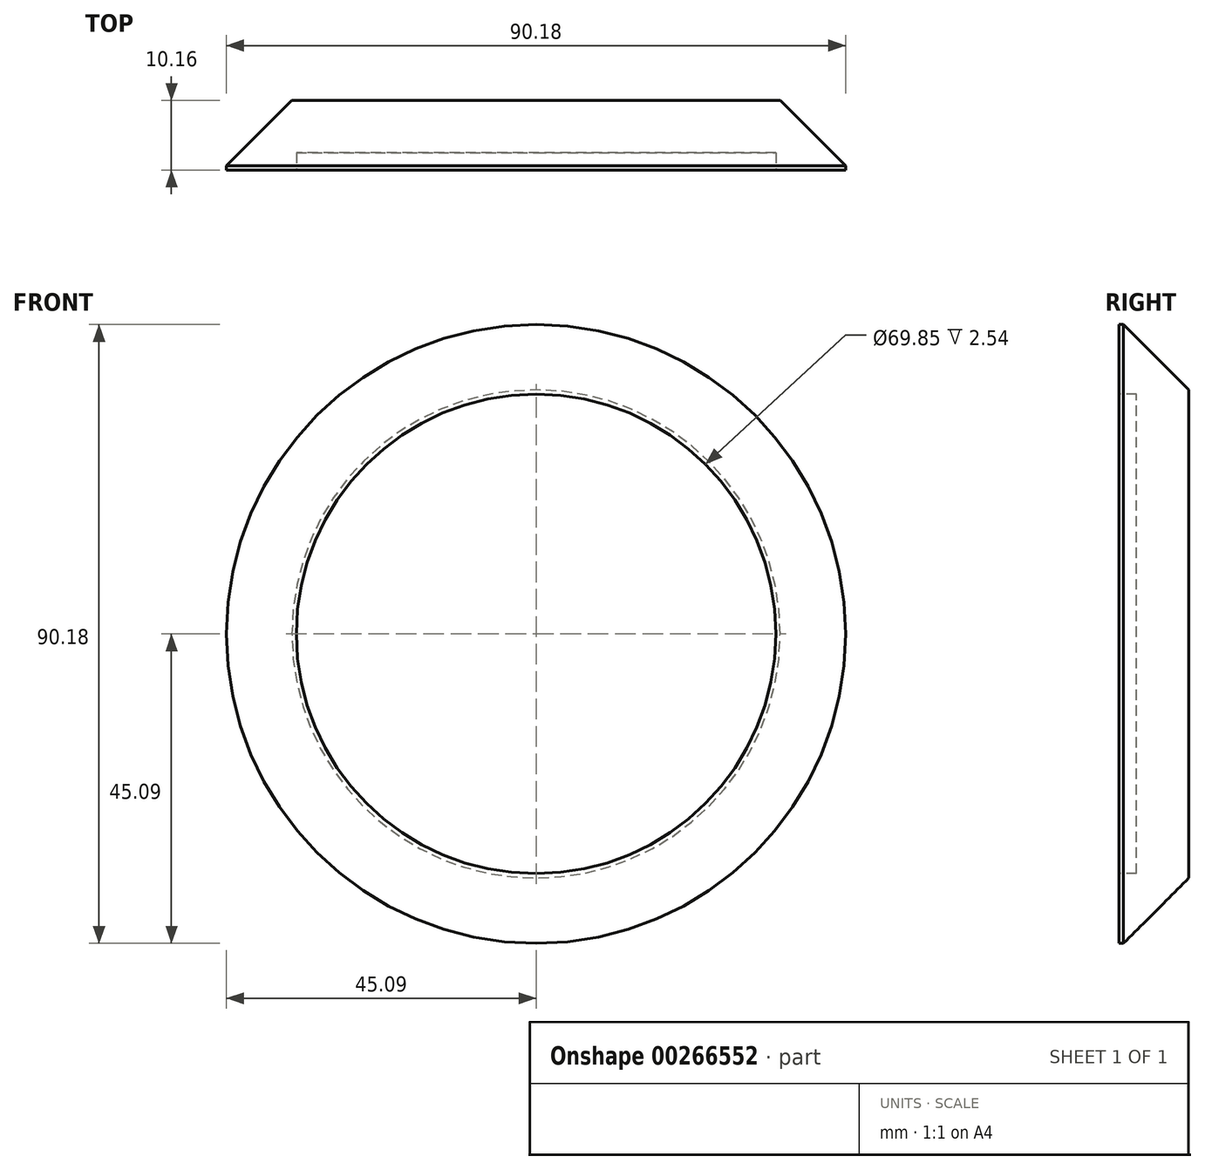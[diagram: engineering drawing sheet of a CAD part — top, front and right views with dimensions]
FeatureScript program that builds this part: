
annotation { "Feature Type Name" : "Feature", "Feature Type Description" : "" }
export const myFeature = defineFeature(function(context is Context, id is Id, definition is map)
    precondition{}
    {
        {
            var Q0;
            Q0=qCreatedBy(makeId("Front.planeOp"),FACE);
            var sketch = newSketch(context, id + "F0", { "sketchPlane" : qUnion([Q0])});
            skCircle(sketch, "E0", {"center": v(0, 0) * mm, "radius": 45.09 * mm});
            skSolve(sketch);
        }
        {
            var Q0;
            Q0=makeQuery(id+"F0.imprint","IMPRINT",FACE,{"disambiguationData":[TD([[makeQuery(id+"F0.imprint","IMPRINT",EDGE,{"derivedFrom":sQuery(id+"F0.wireOp",EDGE,"E0")}),1.0]])]});
            extrude(context, id + "F1", {"entities" : qUnion([Q0]), "depth" : 10.16 * mm});
        }
        {
            var Q0;
            Q0=makeQuery(id+"F1.opExtrude","CAP_FACE",FACE,{"disambiguationData":[OSD([sQuery(id+"F0.wireOp",EDGE,"E0")])],"isStart":false});
            var sketch = newSketch(context, id + "F2", { "sketchPlane" : qUnion([Q0])});
            skCircle(sketch, "E1", {"center": v(0, 0) * mm, "radius": 34.93 * mm});
            skSolve(sketch);
        }
        {
            var Q0;
            Q0=qSketchRegion(id+"F2",true);
            extrude(context, id + "F3", {"entities" : qUnion([Q0]), "operationType" : NewBodyOperationType.REMOVE, "oppositeDirection" : true, "depth" : 2.54 * mm});
        }
        {
            var Q0;
            Q0=makeQuery(id+"F1.opExtrude","CAP_EDGE",EDGE,{"disambiguationData":[OSD([sQuery(id+"F0.wireOp",EDGE,"E0")])],"isStart":true});
            chamfer(context, id + "F4", {"entities" : qUnion([Q0]), "width" : 9.52 * mm, "tangentPropagation" : true});
        }
    });
